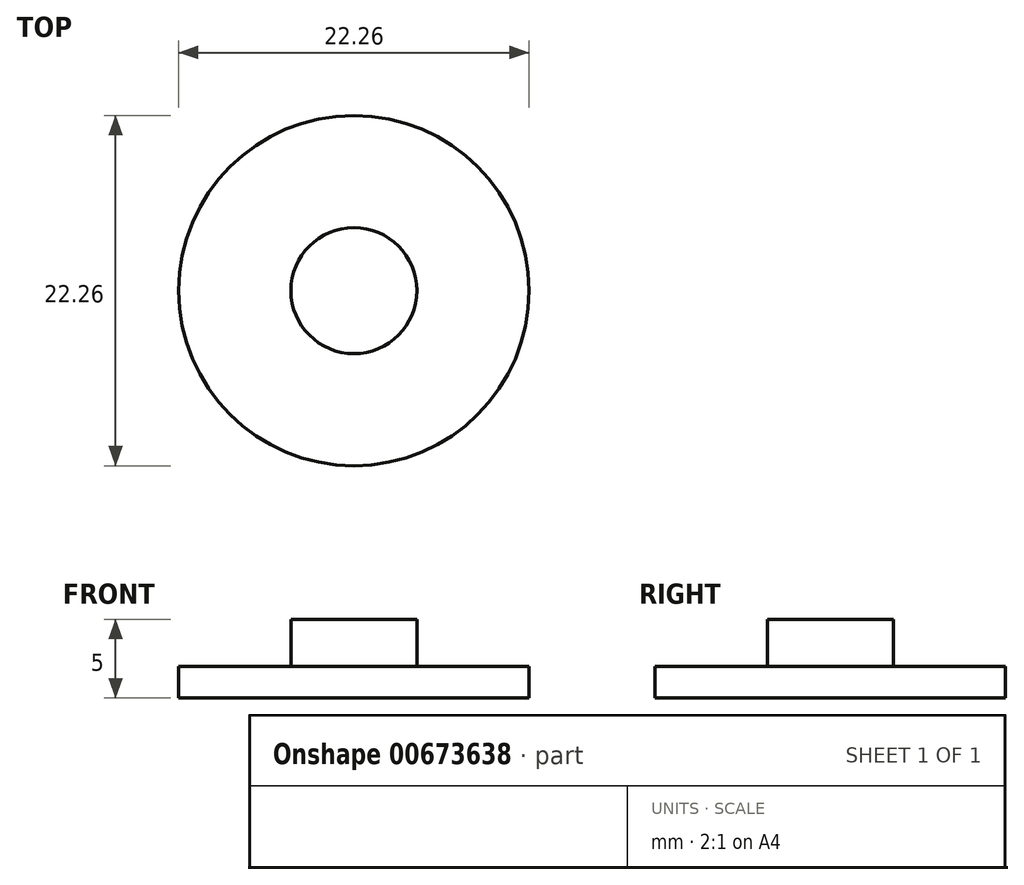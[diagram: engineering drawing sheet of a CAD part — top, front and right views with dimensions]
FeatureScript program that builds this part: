
annotation { "Feature Type Name" : "Feature", "Feature Type Description" : "" }
export const myFeature = defineFeature(function(context is Context, id is Id, definition is map)
    precondition{}
    {
        {
            var Q0;
            Q0=qCreatedBy(makeId("Top.planeOp"),FACE);
            var sketch = newSketch(context, id + "F0", { "sketchPlane" : qUnion([Q0])});
            skCircle(sketch, "E0", {"center": v(0, 0) * mm, "radius": 4 * mm});
            skSolve(sketch);
        }
        {
            var Q0;
            Q0=makeQuery(id+"F0.imprint","IMPRINT",FACE,{"disambiguationData":[TD([[makeQuery(id+"F0.imprint","IMPRINT",EDGE,{"derivedFrom":sQuery(id+"F0.wireOp",EDGE,"E0")}),1.0]])]});
            extrude(context, id + "F1", {"entities" : qUnion([Q0]), "depth" : 3 * mm, "offsetDistance" : 25.4 * mm});
        }
        {
            var Q0;
            Q0=qCreatedBy(makeId("Top.planeOp"),FACE);
            var sketch = newSketch(context, id + "F2", { "sketchPlane" : qUnion([Q0])});
            skCircle(sketch, "E1", {"center": v(0, 0) * mm, "radius": 11.12 * mm});
            skSolve(sketch);
        }
        {
            var Q0;
            Q0=makeQuery(id+"F2.imprint","IMPRINT",FACE,{"disambiguationData":[TD([[makeQuery(id+"F2.imprint","IMPRINT",EDGE,{"derivedFrom":sQuery(id+"F2.wireOp",EDGE,"E1")}),1.0]])]});
            extrude(context, id + "F3", {"entities" : qUnion([Q0]), "operationType" : NewBodyOperationType.ADD, "oppositeDirection" : true, "depth" : 2 * mm, "offsetDistance" : 25.4 * mm});
        }
    });
